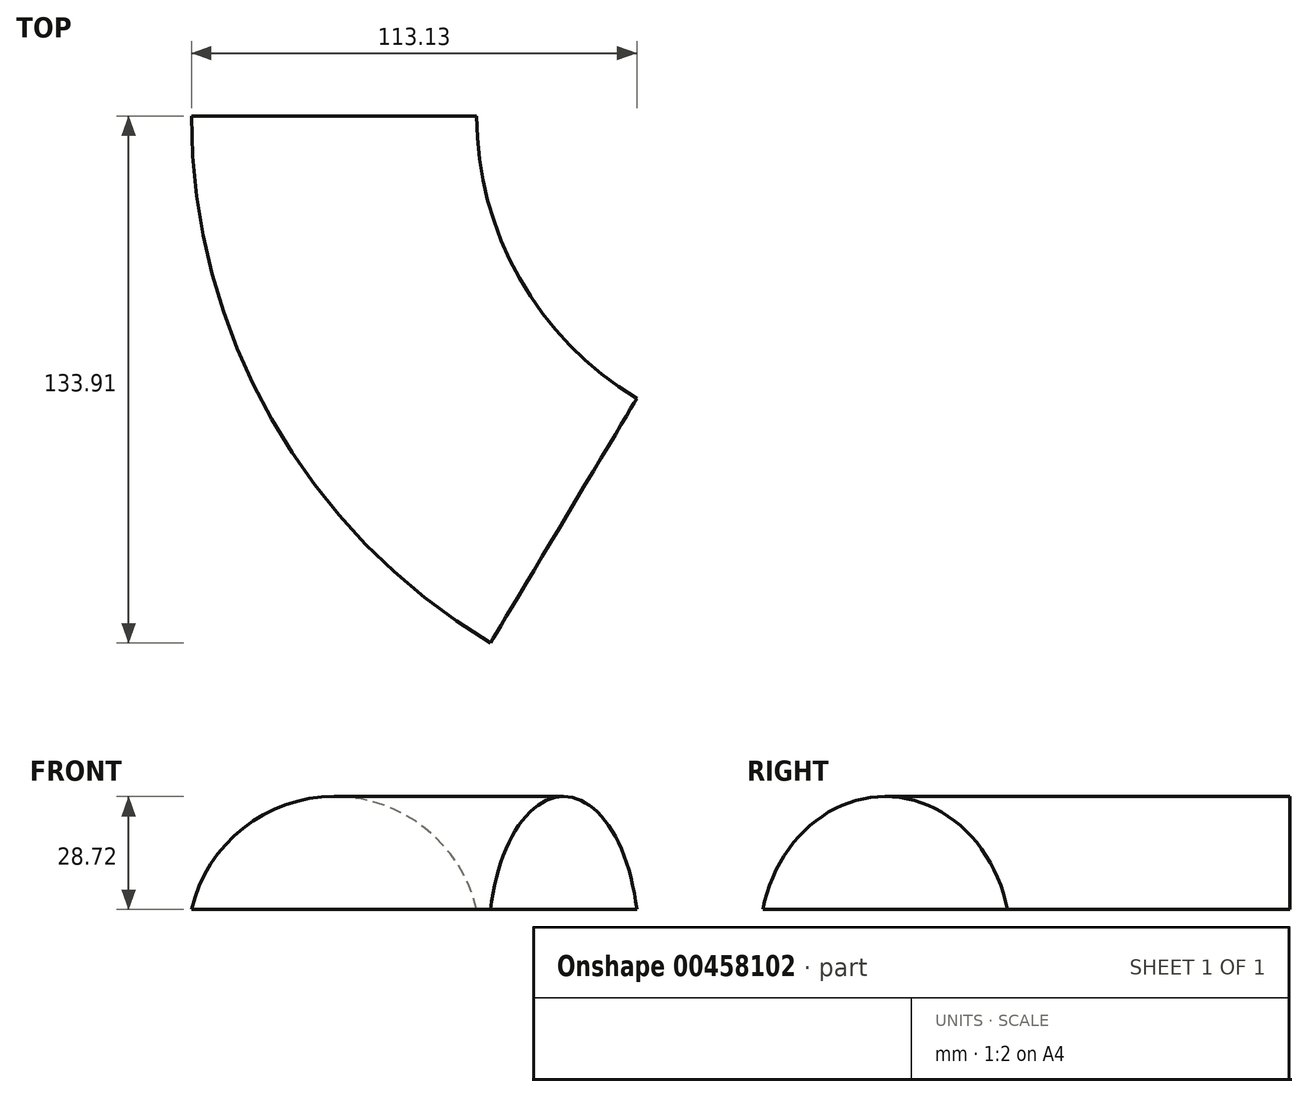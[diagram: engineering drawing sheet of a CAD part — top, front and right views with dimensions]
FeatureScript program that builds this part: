
annotation { "Feature Type Name" : "Feature", "Feature Type Description" : "" }
export const myFeature = defineFeature(function(context is Context, id is Id, definition is map)
    precondition{}
    {
        {
            var Q0;
            Q0=qCreatedBy(makeId("Front.planeOp"),FACE);
            var sketch = newSketch(context, id + "F0", { "sketchPlane" : qUnion([Q0])});
            skLineSegment(sketch, "E0", {"start": v(-37.42, 0) * mm, "end": v(35.03, 0) * mm});
            skArc(sketch, "E1", {"start": v(35.03, 0) * mm, "mid": v(-1.2, 28.72) * mm, "end": v(-37.42, 0) * mm});
            skSolve(sketch);
        }
        {
            var Q0;
            Q0=qCreatedBy(makeId("Top.planeOp"),FACE);
            var sketch = newSketch(context, id + "F1", { "sketchPlane" : qUnion([Q0])});
            skArc(sketch, "E2", {"start": v(0, 0) * mm, "mid": v(15.44, -58.51) * mm, "end": v(57.72, -101.8) * mm});
            skSolve(sketch);
        }
        {
            var Q0;
            Q0=makeQuery(id+"F0.imprint","IMPRINT",FACE,{"disambiguationData":[TD([[makeQuery(id+"F0.imprint","IMPRINT",EDGE,{"derivedFrom":sQuery(id+"F0.wireOp",EDGE,"E0")}),1.0]])]});
            var Q1;
            Q1=sQuery(id+"F1.wireOp",EDGE,"E2");
            sweep(context, id + "F2", {"profiles" : qUnion([Q0]), "path" : qUnion([Q1])});
        }
    });
